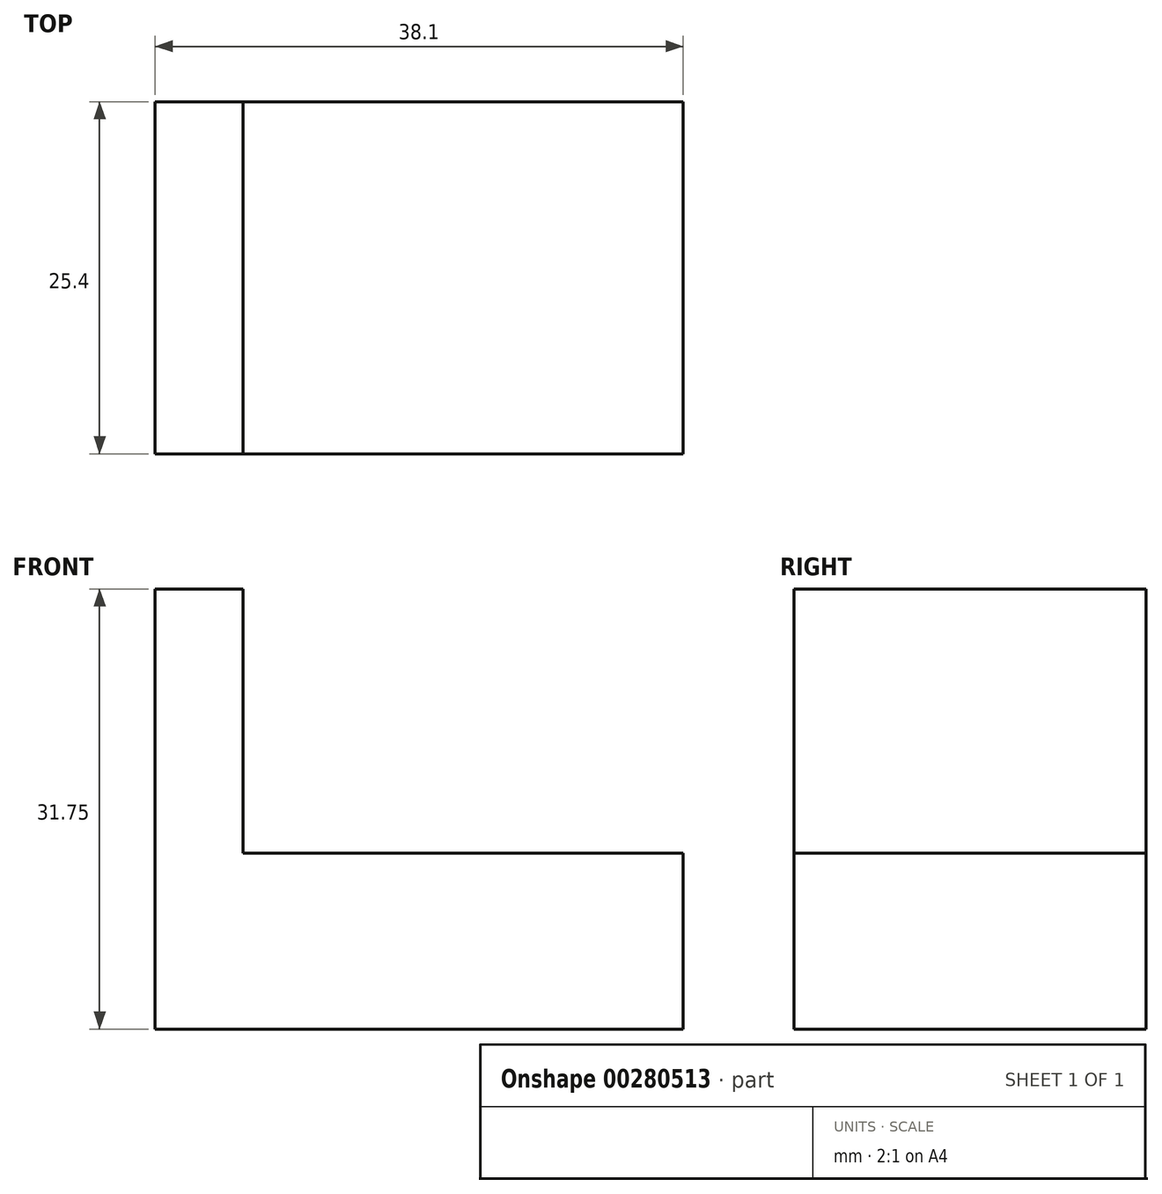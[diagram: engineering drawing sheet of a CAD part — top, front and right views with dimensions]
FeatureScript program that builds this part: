
annotation { "Feature Type Name" : "Feature", "Feature Type Description" : "" }
export const myFeature = defineFeature(function(context is Context, id is Id, definition is map)
    precondition{}
    {
        {
            var Q0;
            Q0=qCreatedBy(makeId("Front.planeOp"),FACE);
            var sketch = newSketch(context, id + "F0", { "sketchPlane" : qUnion([Q0])});
            skLineSegment(sketch, "E0", {"start": v(0, 0) * mm, "end": v(38.1, 0) * mm});
            skLineSegment(sketch, "E1", {"start": v(38.1, 0) * mm, "end": v(38.1, 12.7) * mm});
            skLineSegment(sketch, "E2", {"start": v(38.1, 12.7) * mm, "end": v(6.35, 12.7) * mm});
            skLineSegment(sketch, "E3", {"start": v(6.35, 12.7) * mm, "end": v(6.35, 31.75) * mm});
            skLineSegment(sketch, "E4", {"start": v(6.35, 31.75) * mm, "end": v(0, 31.75) * mm});
            skLineSegment(sketch, "E5", {"start": v(0, 31.75) * mm, "end": v(0, 0) * mm});
            skSolve(sketch);
        }
        {
            var Q0;
            Q0=makeQuery(id+"F0.imprint","IMPRINT",FACE,{"disambiguationData":[TD([[makeQuery(id+"F0.imprint","IMPRINT",EDGE,{"derivedFrom":sQuery(id+"F0.wireOp",EDGE,"E0")}),1.0]])]});
            var Q1;
            Q1 = qSketchRegion(id + "FhupiPMjtVLO8DL_0", true);
            extrude(context, id + "F1", {"entities" : qUnion([Q0, Q1]), "endBound" : BoundingType.SYMMETRIC, "oppositeDirection" : true, "depth" : 25.4 * mm});
        }
    });
